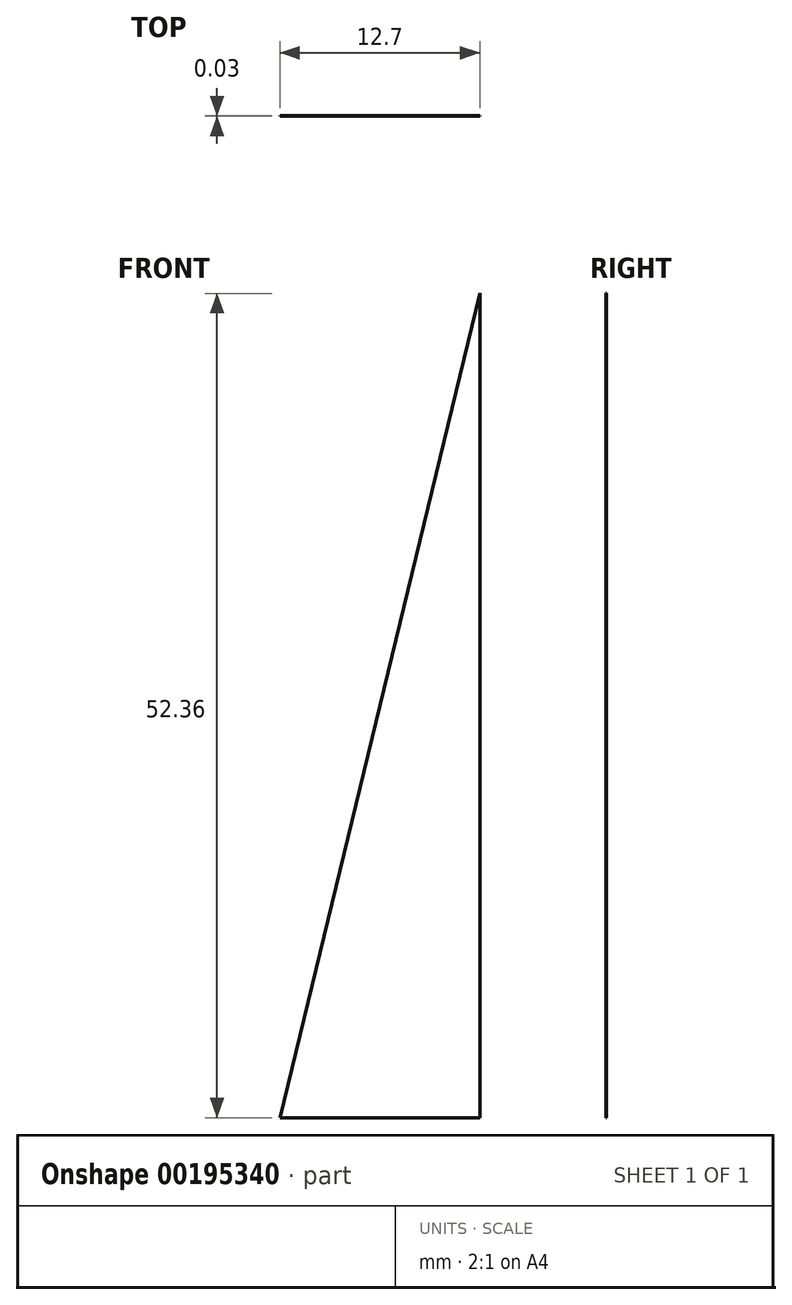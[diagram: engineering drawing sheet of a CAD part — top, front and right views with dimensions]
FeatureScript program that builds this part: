
annotation { "Feature Type Name" : "Feature", "Feature Type Description" : "" }
export const myFeature = defineFeature(function(context is Context, id is Id, definition is map)
    precondition{}
    {
        {
            var Q0;
            Q0=qCreatedBy(makeId("Front.planeOp"),FACE);
            var sketch = newSketch(context, id + "F0", { "sketchPlane" : qUnion([Q0])});
            skLineSegment(sketch, "E0", {"start": v(0, 0) * mm, "end": v(12.7, 0) * mm});
            skLineSegment(sketch, "E1", {"start": v(12.7, 0) * mm, "end": v(12.7, 52.36) * mm});
            skLineSegment(sketch, "E2", {"start": v(12.7, 52.36) * mm, "end": v(0, 0) * mm});
            skSolve(sketch);
        }
        {
            var Q0;
            Q0=makeQuery(id+"F0.imprint","IMPRINT",FACE,{"disambiguationData":[TD([[makeQuery(id+"F0.imprint","IMPRINT",EDGE,{"derivedFrom":sQuery(id+"F0.wireOp",EDGE,"E0")}),1.0]])]});
            extrude(context, id + "F1", {"entities" : qUnion([Q0]), "depth" : 0.03 * mm});
        }
    });
